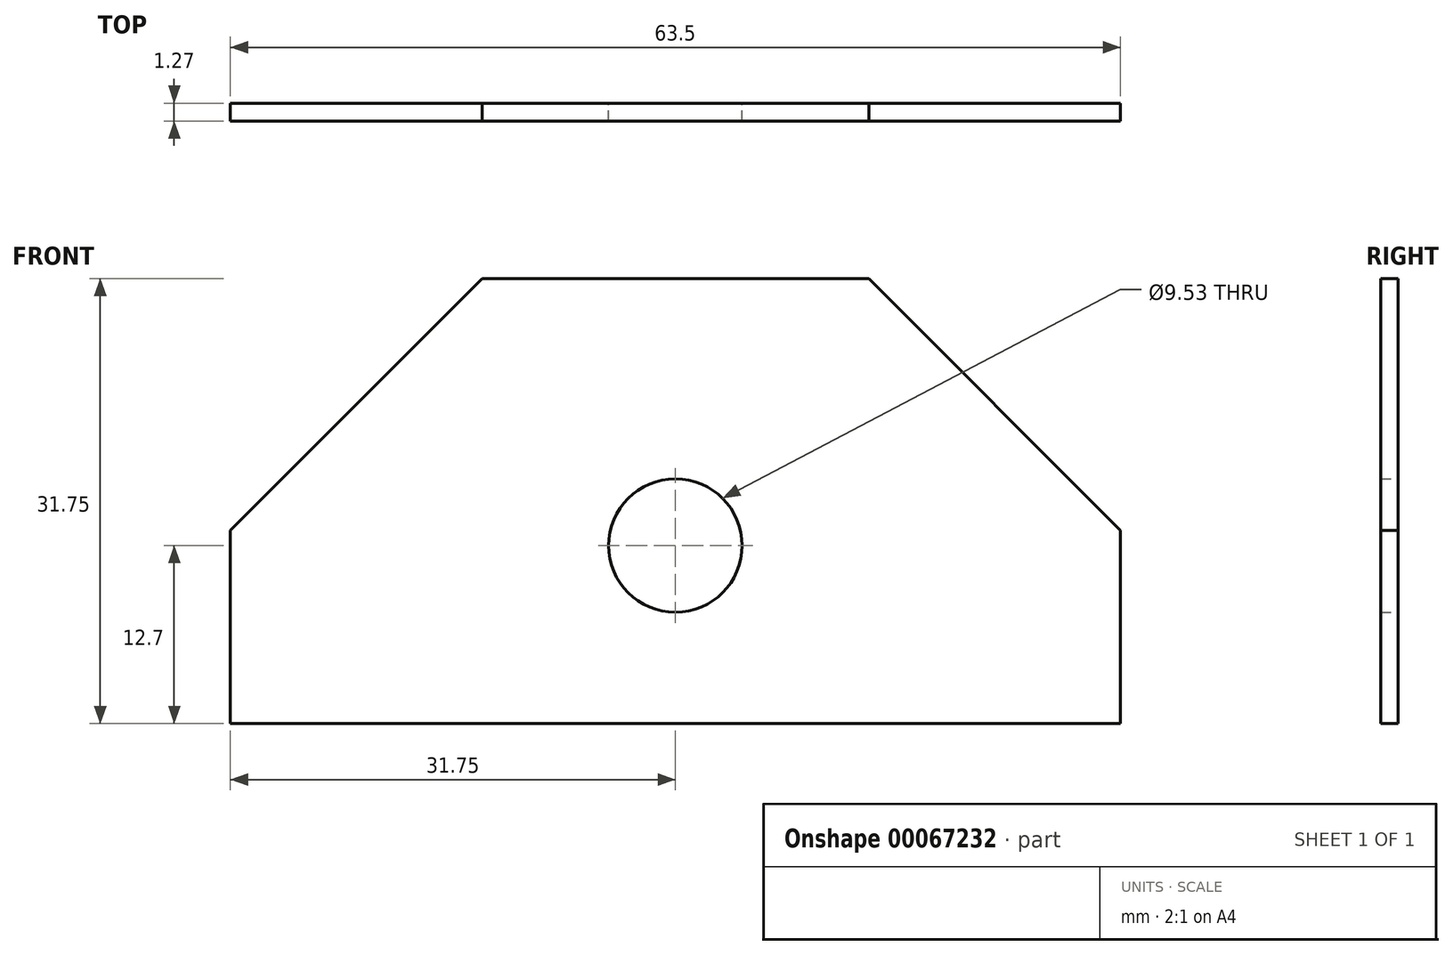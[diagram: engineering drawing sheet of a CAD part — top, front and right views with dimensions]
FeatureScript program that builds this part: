
annotation { "Feature Type Name" : "Feature", "Feature Type Description" : "" }
export const myFeature = defineFeature(function(context is Context, id is Id, definition is map)
    precondition{}
    {
        {
            var Q0;
            Q0=qCreatedBy(makeId("Front.planeOp"),FACE);
            var sketch = newSketch(context, id + "F0", { "sketchPlane" : qUnion([Q0])});
            skLineSegment(sketch, "E0", {"start": v(-31.75, 0) * mm, "end": v(-31.75, 13.79) * mm});
            skLineSegment(sketch, "E1", {"start": v(-31.75, 13.79) * mm, "end": v(-13.79, 31.75) * mm});
            skLineSegment(sketch, "E2", {"start": v(-13.79, 31.75) * mm, "end": v(0, 31.75) * mm});
            skLineSegment(sketch, "E3", {"start": v(0, 31.75) * mm, "end": v(0, 17.46) * mm});
            skLineSegment(sketch, "E4", {"start": v(0, 0) * mm, "end": v(-31.75, 0) * mm});
            skArc(sketch, "E5", {"start": v(0, 17.46) * mm, "mid": v(-4.76, 12.7) * mm, "end": v(0, 7.94) * mm});
            skLineSegment(sketch, "E6.MirrorCS", {"start": v(0, 0) * mm, "end": v(31.75, 0) * mm});
            skArc(sketch, "E7.MirrorCS", {"start": v(0, 17.46) * mm, "mid": v(4.76, 12.7) * mm, "end": v(0, 7.94) * mm});
            skLineSegment(sketch, "E8.MirrorCS", {"start": v(31.75, 13.79) * mm, "end": v(13.79, 31.75) * mm});
            skLineSegment(sketch, "E9.MirrorCS", {"start": v(31.75, 0) * mm, "end": v(31.75, 13.79) * mm});
            skLineSegment(sketch, "E10.MirrorCS", {"start": v(13.79, 31.75) * mm, "end": v(0, 31.75) * mm});
            skLineSegment(sketch, "E11.trimOffspring", {"start": v(0, 12.7) * mm, "end": v(0, 0) * mm});
            skSolve(sketch);
        }
        {
            var Q0;
            Q0=makeQuery(id+"F0.imprint","IMPRINT",FACE,{"disambiguationData":[TD([[makeQuery(id+"F0.imprint","IMPRINT",EDGE,{"derivedFrom":sQuery(id+"F0.wireOp",EDGE,"E0")}),-1.0]])]});
            var Q1;
            {var subQ1=sQuery(id+"F0.wireOp",EDGE,"E6.MirrorCS");Q1=makeQuery(id+"F0.imprint","IMPRINT",FACE,{"disambiguationData":[TD([[makeQuery(id+"F0.imprint","IMPRINT",EDGE,{"derivedFrom":subQ1}),1.0]])]});}
            extrude(context, id + "F1", {"entities" : qUnion([Q0, Q1]), "depth" : 1.27 * mm});
        }
    });
